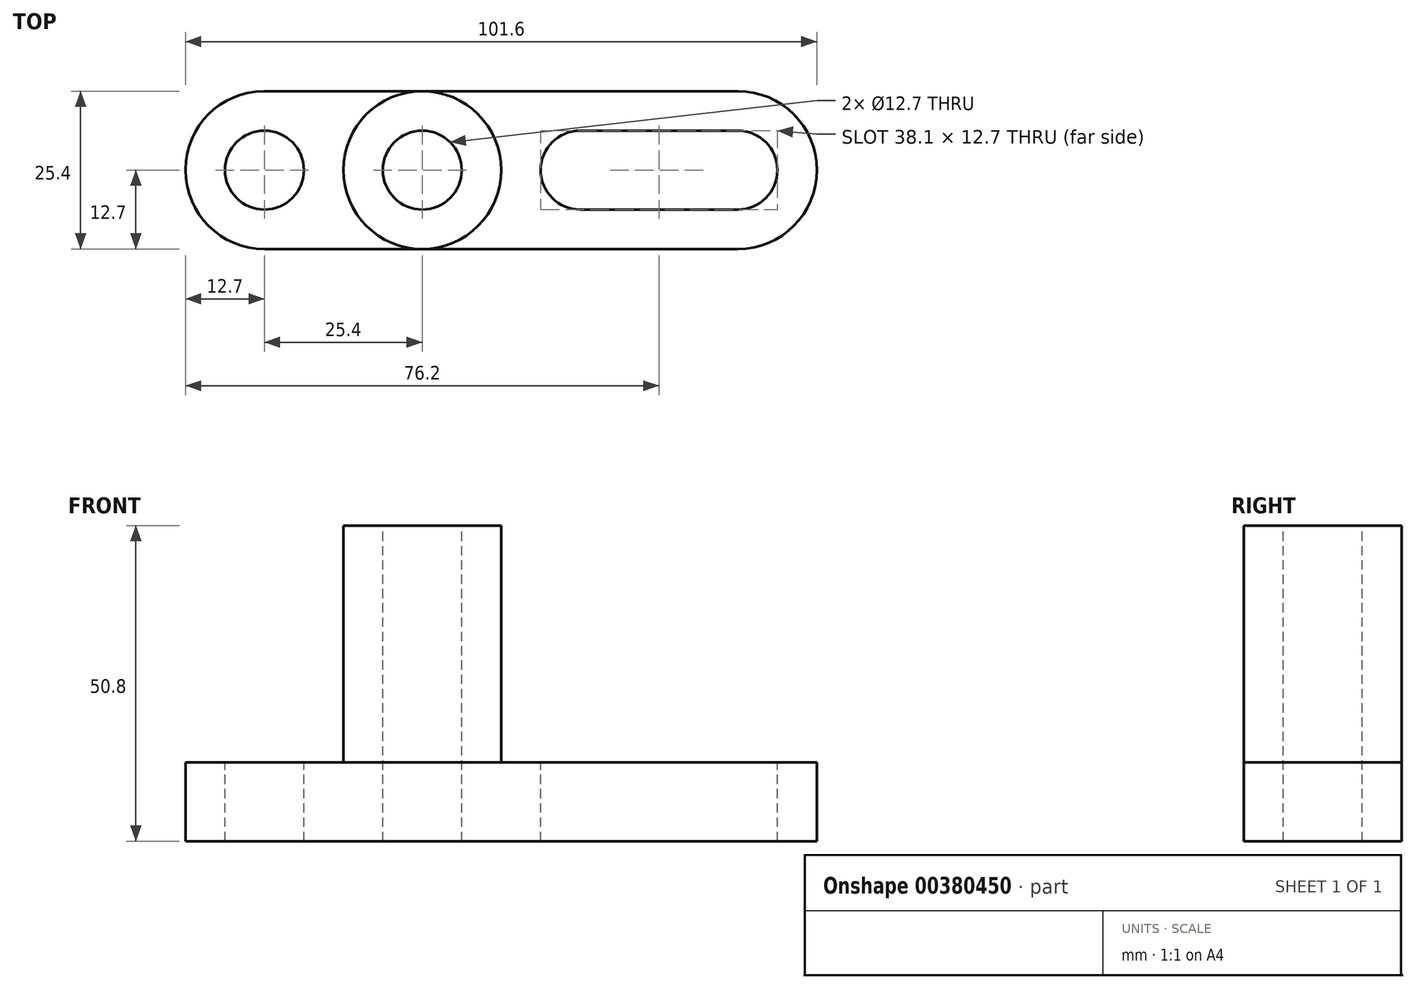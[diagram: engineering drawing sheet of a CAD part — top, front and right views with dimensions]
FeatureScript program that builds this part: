
annotation { "Feature Type Name" : "Feature", "Feature Type Description" : "" }
export const myFeature = defineFeature(function(context is Context, id is Id, definition is map)
    precondition{}
    {
        {
            var Q0;
            Q0=qCreatedBy(makeId("Front.planeOp"),FACE);
            var sketch = newSketch(context, id + "F0", { "sketchPlane" : qUnion([Q0])});
            skLineSegment(sketch, "E0", {"start": v(-101.6, 0) * mm, "end": v(0, 0) * mm});
            skLineSegment(sketch, "E1", {"start": v(0, 0) * mm, "end": v(0, 12.7) * mm});
            skLineSegment(sketch, "E2", {"start": v(0, 12.7) * mm, "end": v(-50.8, 12.7) * mm});
            skLineSegment(sketch, "E3", {"start": v(-50.8, 12.7) * mm, "end": v(-50.8, 50.8) * mm});
            skLineSegment(sketch, "E4", {"start": v(-50.8, 50.8) * mm, "end": v(-76.2, 50.8) * mm});
            skLineSegment(sketch, "E5", {"start": v(-76.2, 50.8) * mm, "end": v(-76.2, 12.7) * mm});
            skLineSegment(sketch, "E6", {"start": v(-76.2, 12.7) * mm, "end": v(-101.6, 12.7) * mm});
            skLineSegment(sketch, "E7", {"start": v(-101.6, 12.7) * mm, "end": v(-101.6, 0) * mm});
            skSolve(sketch);
        }
        {
            var Q0;
            Q0=makeQuery(id+"F0.imprint","IMPRINT",FACE,{"disambiguationData":[TD([[makeQuery(id+"F0.imprint","IMPRINT",EDGE,{"derivedFrom":sQuery(id+"F0.wireOp",EDGE,"E0")}),1.0]])]});
            extrude(context, id + "F1", {"entities" : qUnion([Q0]), "depth" : 25.4 * mm});
        }
        {
            var Q0;
            Q0=makeQuery(id+"F1.opExtrude","SWEPT_FACE",FACE,{"disambiguationData":[OSD([sQuery(id+"F0.wireOp",EDGE,"E2")])]});
            var sketch = newSketch(context, id + "F2", { "sketchPlane" : qUnion([Q0])});
            skCircle(sketch, "E8", {"center": v(-88.9, -12.7) * mm, "radius": 6.35 * mm});
            skCircle(sketch, "E9", {"center": v(-38.1, -12.7) * mm, "radius": 6.35 * mm});
            skCircle(sketch, "E10", {"center": v(-12.7, -12.7) * mm, "radius": 6.35 * mm});
            skLineSegment(sketch, "E11", {"start": v(-38.1, -12.7) * mm, "end": v(-38.1, -6.35) * mm});
            skLineSegment(sketch, "E12", {"start": v(-38.1, -6.35) * mm, "end": v(-12.7, -6.35) * mm});
            skLineSegment(sketch, "E13", {"start": v(-12.7, -6.35) * mm, "end": v(-12.7, -12.7) * mm});
            skLineSegment(sketch, "E14", {"start": v(-12.7, -19.05) * mm, "end": v(-38.1, -19.05) * mm});
            skSolve(sketch);
        }
        {
            var Q0;
            Q0=makeQuery(id+"F2.imprint","IMPRINT",FACE,{"disambiguationData":[TD([[makeQuery(id+"F2.imprint","IMPRINT",EDGE,{"derivedFrom":sQuery(id+"F2.wireOp",EDGE,"E8")}),1.0]])]});
            var Q1;
            {var subQ0=sQuery(id+"F2.wireOp",EDGE,"E12");Q1=makeQuery(id+"F2.imprint","IMPRINT",FACE,{"disambiguationData":[TD([[makeQuery(id+"F2.imprint","IMPRINT",EDGE,{"derivedFrom":subQ0}),-1.0]])]});}
            var Q2;
            {var subQ0=sQuery(id+"F2.wireOp",EDGE,"E9");var subQ1=makeQuery(id+"F2.imprint","INTERSECT",VERTEX,{"derivedFrom":[subQ0,sQuery(id+"F2.wireOp",EDGE,"E12")]});Q2=makeQuery(id+"F2.imprint","IMPRINT",FACE,{"disambiguationData":[TD([[makeQuery(id+"F2.imprint","IMPRINT",EDGE,{"disambiguationData":[TD([[subQ1,-1.0]])],"derivedFrom":subQ0}),1.0]])]});}
            var Q3;
            {var subQ0=sQuery(id+"F2.wireOp",EDGE,"E10");var subQ1=makeQuery(id+"F2.imprint","INTERSECT",VERTEX,{"derivedFrom":[subQ0,sQuery(id+"F2.wireOp",EDGE,"E12")]});Q3=makeQuery(id+"F2.imprint","IMPRINT",FACE,{"disambiguationData":[TD([[makeQuery(id+"F2.imprint","IMPRINT",EDGE,{"disambiguationData":[TD([[subQ1,-1.0]])],"derivedFrom":subQ0}),1.0]])]});}
            extrude(context, id + "F3", {"entities" : qUnion([Q0, Q1, Q2, Q3]), "operationType" : NewBodyOperationType.REMOVE, "oppositeDirection" : true, "depth" : 25.4 * mm});
        }
        {
            var Q0;
            Q0=makeQuery(id+"F1.opExtrude","SWEPT_FACE",FACE,{"disambiguationData":[OSD([sQuery(id+"F0.wireOp",EDGE,"E4")])]});
            var sketch = newSketch(context, id + "F4", { "sketchPlane" : qUnion([Q0])});
            skCircle(sketch, "E15", {"center": v(-63.5, -12.7) * mm, "radius": 6.35 * mm});
            skSolve(sketch);
        }
        {
            var Q0;
            Q0=makeQuery(id+"F4.imprint","IMPRINT",FACE,{"disambiguationData":[TD([[makeQuery(id+"F4.imprint","IMPRINT",EDGE,{"derivedFrom":sQuery(id+"F4.wireOp",EDGE,"E15")}),1.0]])]});
            var Q1;
            Q1=sQuery(id+"F4.wireOp",EDGE,"E15");
            extrude(context, id + "F5", {"entities" : qUnion([Q0]), "operationType" : NewBodyOperationType.REMOVE, "surfaceEntities" : qUnion([Q1]), "oppositeDirection" : true, "depth" : 50.8 * mm});
        }
        {
            var Q0;
            Q0=makeQuery(id+"F1.opExtrude","SWEPT_FACE",FACE,{"disambiguationData":[OSD([sQuery(id+"F0.wireOp",EDGE,"E6")])]});
            var sketch = newSketch(context, id + "F6", { "sketchPlane" : qUnion([Q0])});
            skArc(sketch, "E16", {"start": v(-101.6, -12.7) * mm, "mid": v(-97.88, -21.68) * mm, "end": v(-88.9, -25.4) * mm});
            skArc(sketch, "E17", {"start": v(-88.9, 0) * mm, "mid": v(-97.9, -3.7) * mm, "end": v(-101.6, -12.7) * mm});
            skLineSegment(sketch, "E18", {"start": v(-101.6, -12.7) * mm, "end": v(-101.6, 0) * mm});
            skLineSegment(sketch, "E19", {"start": v(-101.6, 0) * mm, "end": v(-88.9, 0) * mm});
            skLineSegment(sketch, "E20", {"start": v(-101.6, -12.7) * mm, "end": v(-101.6, -25.4) * mm});
            skLineSegment(sketch, "E21", {"start": v(-101.6, -25.4) * mm, "end": v(-88.9, -25.4) * mm});
            skSolve(sketch);
        }
        {
            var Q0;
            Q0=makeQuery(id+"F6.imprint","IMPRINT",FACE,{"disambiguationData":[TD([[makeQuery(id+"F6.imprint","IMPRINT",EDGE,{"derivedFrom":sQuery(id+"F6.wireOp",EDGE,"E16")}),-1.0]])]});
            var Q1;
            {var subQ0=sQuery(id+"F6.wireOp",EDGE,"E19");var subQ1=sQuery(id+"F6.wireOp",EDGE,"E17");var subQ2=makeQuery(id+"F6.imprint","INTERSECT",VERTEX,{"derivedFrom":[subQ1,subQ0]});Q1=makeQuery(id+"F6.imprint","IMPRINT",FACE,{"disambiguationData":[TD([[makeQuery(id+"F6.imprint","IMPRINT",EDGE,{"disambiguationData":[TD([[subQ2,-1.0]])],"derivedFrom":subQ1}),-1.0]])]});}
            extrude(context, id + "F7", {"entities" : qUnion([Q0, Q1]), "operationType" : NewBodyOperationType.REMOVE, "oppositeDirection" : true, "depth" : 25.4 * mm});
        }
        {
            var Q0;
            Q0=makeQuery(id+"F1.opExtrude","SWEPT_FACE",FACE,{"disambiguationData":[OSD([sQuery(id+"F0.wireOp",EDGE,"E4")])]});
            var sketch = newSketch(context, id + "F8", { "sketchPlane" : qUnion([Q0])});
            skArc(sketch, "E22", {"start": v(-63.5, 0) * mm, "mid": v(-72.48, -3.72) * mm, "end": v(-76.2, -12.7) * mm});
            skArc(sketch, "E23", {"start": v(-50.8, -12.7) * mm, "mid": v(-54.52, -3.72) * mm, "end": v(-63.5, 0) * mm});
            skArc(sketch, "E24", {"start": v(-63.5, -25.4) * mm, "mid": v(-54.52, -21.68) * mm, "end": v(-50.8, -12.7) * mm});
            skArc(sketch, "E25", {"start": v(-76.2, -12.7) * mm, "mid": v(-72.48, -21.68) * mm, "end": v(-63.5, -25.4) * mm});
            skLineSegment(sketch, "E26", {"start": v(-76.2, -12.7) * mm, "end": v(-76.2, 0) * mm});
            skLineSegment(sketch, "E27", {"start": v(-76.2, 0) * mm, "end": v(-63.5, 0) * mm});
            skLineSegment(sketch, "E28", {"start": v(-50.8, 0) * mm, "end": v(-50.8, -12.7) * mm});
            skLineSegment(sketch, "E29", {"start": v(-50.8, -25.4) * mm, "end": v(-63.5, -25.4) * mm});
            skLineSegment(sketch, "E30", {"start": v(-76.2, -25.4) * mm, "end": v(-76.2, -12.7) * mm});
            skSolve(sketch);
        }
        {
            var Q0;
            Q0=makeQuery(id+"F8.imprint","IMPRINT",FACE,{"disambiguationData":[TD([[makeQuery(id+"F8.imprint","IMPRINT",EDGE,{"derivedFrom":sQuery(id+"F8.wireOp",EDGE,"E22")}),-1.0]])]});
            var Q1;
            {var subQ0=sQuery(id+"F8.wireOp",EDGE,"E23");Q1=makeQuery(id+"F8.imprint","IMPRINT",FACE,{"disambiguationData":[TD([[makeQuery(id+"F8.imprint","IMPRINT",EDGE,{"derivedFrom":subQ0}),-1.0]])]});}
            var Q2;
            {var subQ0=sQuery(id+"F8.wireOp",EDGE,"E24");Q2=makeQuery(id+"F8.imprint","IMPRINT",FACE,{"disambiguationData":[TD([[makeQuery(id+"F8.imprint","IMPRINT",EDGE,{"derivedFrom":subQ0}),-1.0]])]});}
            var Q3;
            {var subQ0=sQuery(id+"F8.wireOp",EDGE,"E25");Q3=makeQuery(id+"F8.imprint","IMPRINT",FACE,{"disambiguationData":[TD([[makeQuery(id+"F8.imprint","IMPRINT",EDGE,{"derivedFrom":subQ0}),-1.0]])]});}
            extrude(context, id + "F9", {"entities" : qUnion([Q0, Q1, Q2, Q3]), "operationType" : NewBodyOperationType.REMOVE, "oppositeDirection" : true, "depth" : 38.1 * mm});
        }
        {
            var Q0;
            {var subQ0=sQuery(id+"F0.wireOp",EDGE,"E4");Q0=makeQuery(id+"F9.boolean.opBoolean","MERGE",FACE,{"derivedFrom":[makeQuery(id+"F1.opExtrude","SWEPT_FACE",FACE,{"disambiguationData":[OSD([sQuery(id+"F0.wireOp",EDGE,"E2")])]}),makeQuery(id+"F9.opExtrude","CAP_FACE",FACE,{"disambiguationData":[OSD([subQ0,sQuery(id+"F8.wireOp",EDGE,"E23"),sQuery(id+"F8.wireOp",EDGE,"E28")])],"isStart":false}),makeQuery(id+"F9.opExtrude","CAP_FACE",FACE,{"disambiguationData":[OSD([sQuery(id+"F0.wireOp",EDGE,"E3"),subQ0,sQuery(id+"F8.wireOp",EDGE,"E24"),sQuery(id+"F8.wireOp",EDGE,"E29")])],"isStart":false})]});}
            var sketch = newSketch(context, id + "F10", { "sketchPlane" : qUnion([Q0])});
            skArc(sketch, "E31", {"start": v(-12.7, -25.4) * mm, "mid": v(-3.72, -21.68) * mm, "end": v(0, -12.7) * mm});
            skArc(sketch, "E32", {"start": v(0, -12.7) * mm, "mid": v(-3.72, -3.72) * mm, "end": v(-12.7, 0) * mm});
            skLineSegment(sketch, "E33", {"start": v(-12.7, 0) * mm, "end": v(0, 0) * mm});
            skLineSegment(sketch, "E34", {"start": v(0, 0) * mm, "end": v(0, -12.7) * mm});
            skLineSegment(sketch, "E35", {"start": v(0, -25.4) * mm, "end": v(-12.7, -25.4) * mm});
            skSolve(sketch);
        }
        {
            var Q0;
            {var subQ0=sQuery(id+"F10.wireOp",EDGE,"E31");Q0=makeQuery(id+"F10.imprint","IMPRINT",FACE,{"disambiguationData":[TD([[makeQuery(id+"F10.imprint","IMPRINT",EDGE,{"derivedFrom":subQ0}),-1.0]])]});}
            var Q1;
            Q1=makeQuery(id+"F10.imprint","IMPRINT",FACE,{"disambiguationData":[TD([[makeQuery(id+"F10.imprint","IMPRINT",EDGE,{"derivedFrom":sQuery(id+"F10.wireOp",EDGE,"E32")}),-1.0]])]});
            extrude(context, id + "F11", {"entities" : qUnion([Q0, Q1]), "operationType" : NewBodyOperationType.REMOVE, "oppositeDirection" : true, "depth" : 25.4 * mm});
        }
        {
            var Q0;
            Q0=makeQuery(id+"F4.imprint","IMPRINT",FACE,{"disambiguationData":[TD([[makeQuery(id+"F4.imprint","IMPRINT",EDGE,{"derivedFrom":sQuery(id+"F4.wireOp",EDGE,"E15")}),1.0]])]});
            var Q1;
            Q1=sQuery(id+"F4.wireOp",EDGE,"E15");
            extrude(context, id + "F12", {"entities" : qUnion([Q0]), "operationType" : NewBodyOperationType.REMOVE, "surfaceEntities" : qUnion([Q1]), "oppositeDirection" : true, "depth" : 50.8 * mm});
        }
    });
